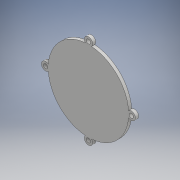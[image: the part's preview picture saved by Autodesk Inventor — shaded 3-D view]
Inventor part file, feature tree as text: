
AUTODESK INVENTOR PART (.ipt)
format: ipt  version: 2018 (Build 220112000, 112)  size: 116,736 bytes
history: native  units: mm
features: extrude x1, sketch x1
ambient origin geometry x8: Origin, YZ Plane, XZ Plane, XY Plane, X Axis, Y Axis, Z Axis, Center Point
bodies: Solid1 (feature_tree)
feature tree (2):
  extrude  "Extrusion1"  [1 undecoded]
  sketch  "Sketch1"  dims[d0=1.5mm d1=0.0mm]
note: 1 required parameter value undecoded (feature->parameter linkage not recoverable at this tier; creation-order binding heuristic only, values carry confidence <= 0.55)
